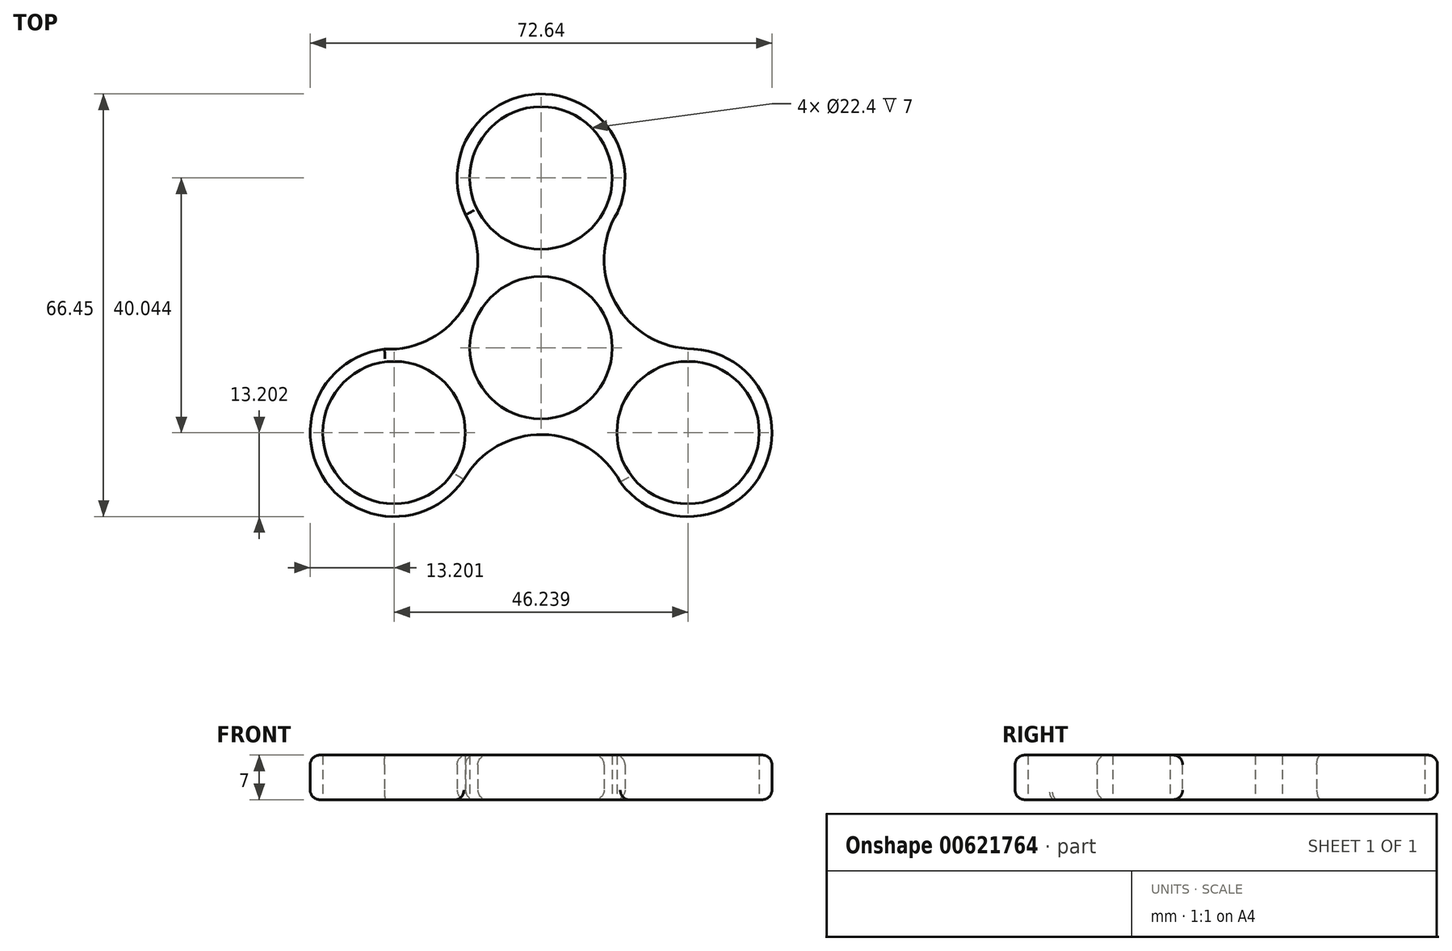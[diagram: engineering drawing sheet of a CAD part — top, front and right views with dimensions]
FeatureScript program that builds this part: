
annotation { "Feature Type Name" : "Feature", "Feature Type Description" : "" }
export const myFeature = defineFeature(function(context is Context, id is Id, definition is map)
    precondition{}
    {
        {
            var Q0;
            Q0=qCreatedBy(makeId("Top.planeOp"),FACE);
            var sketch = newSketch(context, id + "F0", { "sketchPlane" : qUnion([Q0])});
            skCircle(sketch, "E0", {"center": v(0, 0) * mm, "radius": 11.2 * mm});
            skCircle(sketch, "E1", {"center": v(0, 26.7) * mm, "radius": 11.2 * mm});
            skArc(sketch, "E2", {"start": v(11.11, 19.57) * mm, "mid": v(0.27, 39.9) * mm, "end": v(-11.4, 20.03) * mm});
            skArc(sketch, "E3.1.0", {"start": v(-22.5, -0.16) * mm, "mid": v(-34.68, -19.71) * mm, "end": v(-11.65, -19.89) * mm});
            skCircle(sketch, "E3.1.1", {"center": v(-23.12, -13.35) * mm, "radius": 11.2 * mm});
            skArc(sketch, "E3.2.0", {"start": v(11.4, -19.4) * mm, "mid": v(34.41, -20.18) * mm, "end": v(23.05, -0.15) * mm});
            skCircle(sketch, "E3.2.1", {"center": v(23.12, -13.35) * mm, "radius": 11.2 * mm});
            skArc(sketch, "E4", {"start": v(12.1, 21.43) * mm, "mid": v(11.67, 7.1) * mm, "end": v(24.03, -0.18) * mm});
            skArc(sketch, "E5.1.0", {"start": v(-24.61, -0.23) * mm, "mid": v(-11.98, 6.56) * mm, "end": v(-11.86, 20.9) * mm});
            skArc(sketch, "E5.2.0", {"start": v(12.5, -21.2) * mm, "mid": v(0.3, -13.65) * mm, "end": v(-12.17, -20.72) * mm});
            skSolve(sketch);
        }
        {
            var Q0;
            Q0=makeQuery(id+"F0.imprint","IMPRINT",FACE,{"disambiguationData":[TD([[makeQuery(id+"F0.imprint","IMPRINT",EDGE,{"derivedFrom":sQuery(id+"F0.wireOp",EDGE,"E0")}),-1.0]])]});
            extrude(context, id + "F1", {"entities" : qUnion([Q0]), "depth" : 7 * mm, "offsetDistance" : 25 * mm});
        }
        {
            var Q0;
            Q0=makeQuery(id+"F1.opExtrude","CAP_EDGE",EDGE,{"disambiguationData":[OSD([sQuery(id+"F0.wireOp",EDGE,"E5.2.0")])],"isStart":true});
            fillet(context, id + "F2", {"entities" : qUnion([Q0]), "radius" : 1.5 * mm, "tangentPropagation" : true, "allowEdgeOverflow" : false});
        }
        {
            var Q0;
            Q0=makeQuery(id+"F1.opExtrude","SWEPT_FACE",FACE,{"disambiguationData":[OSD([sQuery(id+"F0.wireOp",EDGE,"E4")])]});
            var Q1;
            Q1=makeQuery(id+"F1.opExtrude","CAP_EDGE",EDGE,{"disambiguationData":[OSD([sQuery(id+"F0.wireOp",EDGE,"E4")])],"isStart":true});
            var Q2;
            Q2=makeQuery(id+"F1.opExtrude","CAP_EDGE",EDGE,{"disambiguationData":[OSD([sQuery(id+"F0.wireOp",EDGE,"E3.2.0")])],"isStart":false});
            var Q3;
            Q3=makeQuery(id+"F1.opExtrude","CAP_EDGE",EDGE,{"disambiguationData":[OSD([sQuery(id+"F0.wireOp",EDGE,"E5.2.0")])],"isStart":false});
            var Q4;
            Q4=makeQuery(id+"F1.opExtrude","CAP_EDGE",EDGE,{"disambiguationData":[OSD([sQuery(id+"F0.wireOp",EDGE,"E3.1.0")])],"isStart":false});
            var Q5;
            Q5=makeQuery(id+"F1.opExtrude","CAP_EDGE",EDGE,{"disambiguationData":[OSD([sQuery(id+"F0.wireOp",EDGE,"E5.1.0")])],"isStart":false});
            var Q6;
            Q6=makeQuery(id+"F1.opExtrude","CAP_EDGE",EDGE,{"disambiguationData":[OSD([sQuery(id+"F0.wireOp",EDGE,"E2")])],"isStart":false});
            fillet(context, id + "F3", {"entities" : qUnion([Q0, Q1, Q2, Q3, Q4, Q5, Q6]), "radius" : 1.5 * mm, "tangentPropagation" : true, "allowEdgeOverflow" : false});
        }
        {
            var Q0;
            Q0=makeQuery(id+"F1.opExtrude","CAP_EDGE",EDGE,{"disambiguationData":[OSD([sQuery(id+"F0.wireOp",EDGE,"E2")])],"isStart":true});
            var Q1;
            Q1=makeQuery(id+"F1.opExtrude","CAP_EDGE",EDGE,{"disambiguationData":[OSD([sQuery(id+"F0.wireOp",EDGE,"E5.1.0")])],"isStart":true});
            var Q2;
            Q2=makeQuery(id+"F1.opExtrude","CAP_EDGE",EDGE,{"disambiguationData":[OSD([sQuery(id+"F0.wireOp",EDGE,"E3.1.0")])],"isStart":true});
            var Q3;
            {var subQ0=sQuery(id+"F0.wireOp",EDGE,"E5.2.0");Q3=makeQuery(id+"F2.opFillet","BLEND_EDGE",EDGE,{"blendedFrom":[makeQuery(id+"F1.opExtrude","CAP_EDGE",EDGE,{"disambiguationData":[OSD([subQ0])],"isStart":true}),makeQuery(id+"F1.opExtrude","CAP_FACE",FACE,{"disambiguationData":[OSD([sQuery(id+"F0.wireOp",EDGE,"E0"),sQuery(id+"F0.wireOp",EDGE,"E1"),sQuery(id+"F0.wireOp",EDGE,"E2"),sQuery(id+"F0.wireOp",EDGE,"E3.1.0"),sQuery(id+"F0.wireOp",EDGE,"E3.1.1"),sQuery(id+"F0.wireOp",EDGE,"E3.2.0"),sQuery(id+"F0.wireOp",EDGE,"E3.2.1"),sQuery(id+"F0.wireOp",EDGE,"E4"),sQuery(id+"F0.wireOp",EDGE,"E5.1.0"),subQ0])],"isStart":true})],"blendedInto":[makeQuery(id+"F1.opExtrude","CAP_FACE",FACE,{"disambiguationData":[OSD([sQuery(id+"F0.wireOp",EDGE,"E0"),sQuery(id+"F0.wireOp",EDGE,"E1"),sQuery(id+"F0.wireOp",EDGE,"E2"),sQuery(id+"F0.wireOp",EDGE,"E3.1.0"),sQuery(id+"F0.wireOp",EDGE,"E3.1.1"),sQuery(id+"F0.wireOp",EDGE,"E3.2.0"),sQuery(id+"F0.wireOp",EDGE,"E3.2.1"),sQuery(id+"F0.wireOp",EDGE,"E4"),sQuery(id+"F0.wireOp",EDGE,"E5.1.0"),subQ0])],"isStart":true})]});}
            var Q4;
            Q4=makeQuery(id+"F1.opExtrude","CAP_EDGE",EDGE,{"disambiguationData":[OSD([sQuery(id+"F0.wireOp",EDGE,"E3.2.0")])],"isStart":true});
            var Q5;
            {var subQ0=sQuery(id+"F0.wireOp",EDGE,"E4");Q5=makeQuery(id+"F3.opFillet","BLEND_EDGE",EDGE,{"blendedFrom":[makeQuery(id+"F1.opExtrude","CAP_EDGE",EDGE,{"disambiguationData":[OSD([subQ0])],"isStart":true}),makeQuery(id+"F1.opExtrude","CAP_FACE",FACE,{"disambiguationData":[OSD([sQuery(id+"F0.wireOp",EDGE,"E0"),sQuery(id+"F0.wireOp",EDGE,"E1"),sQuery(id+"F0.wireOp",EDGE,"E2"),sQuery(id+"F0.wireOp",EDGE,"E3.1.0"),sQuery(id+"F0.wireOp",EDGE,"E3.1.1"),sQuery(id+"F0.wireOp",EDGE,"E3.2.0"),sQuery(id+"F0.wireOp",EDGE,"E3.2.1"),subQ0,sQuery(id+"F0.wireOp",EDGE,"E5.1.0"),sQuery(id+"F0.wireOp",EDGE,"E5.2.0")])],"isStart":true})],"blendedInto":[makeQuery(id+"F1.opExtrude","CAP_FACE",FACE,{"disambiguationData":[OSD([sQuery(id+"F0.wireOp",EDGE,"E0"),sQuery(id+"F0.wireOp",EDGE,"E1"),sQuery(id+"F0.wireOp",EDGE,"E2"),sQuery(id+"F0.wireOp",EDGE,"E3.1.0"),sQuery(id+"F0.wireOp",EDGE,"E3.1.1"),sQuery(id+"F0.wireOp",EDGE,"E3.2.0"),sQuery(id+"F0.wireOp",EDGE,"E3.2.1"),subQ0,sQuery(id+"F0.wireOp",EDGE,"E5.1.0"),sQuery(id+"F0.wireOp",EDGE,"E5.2.0")])],"isStart":true})]});}
            fillet(context, id + "F4", {"entities" : qUnion([Q0, Q1, Q2, Q3, Q4, Q5]), "radius" : 1.5 * mm, "tangentPropagation" : true, "allowEdgeOverflow" : false});
        }
    });
